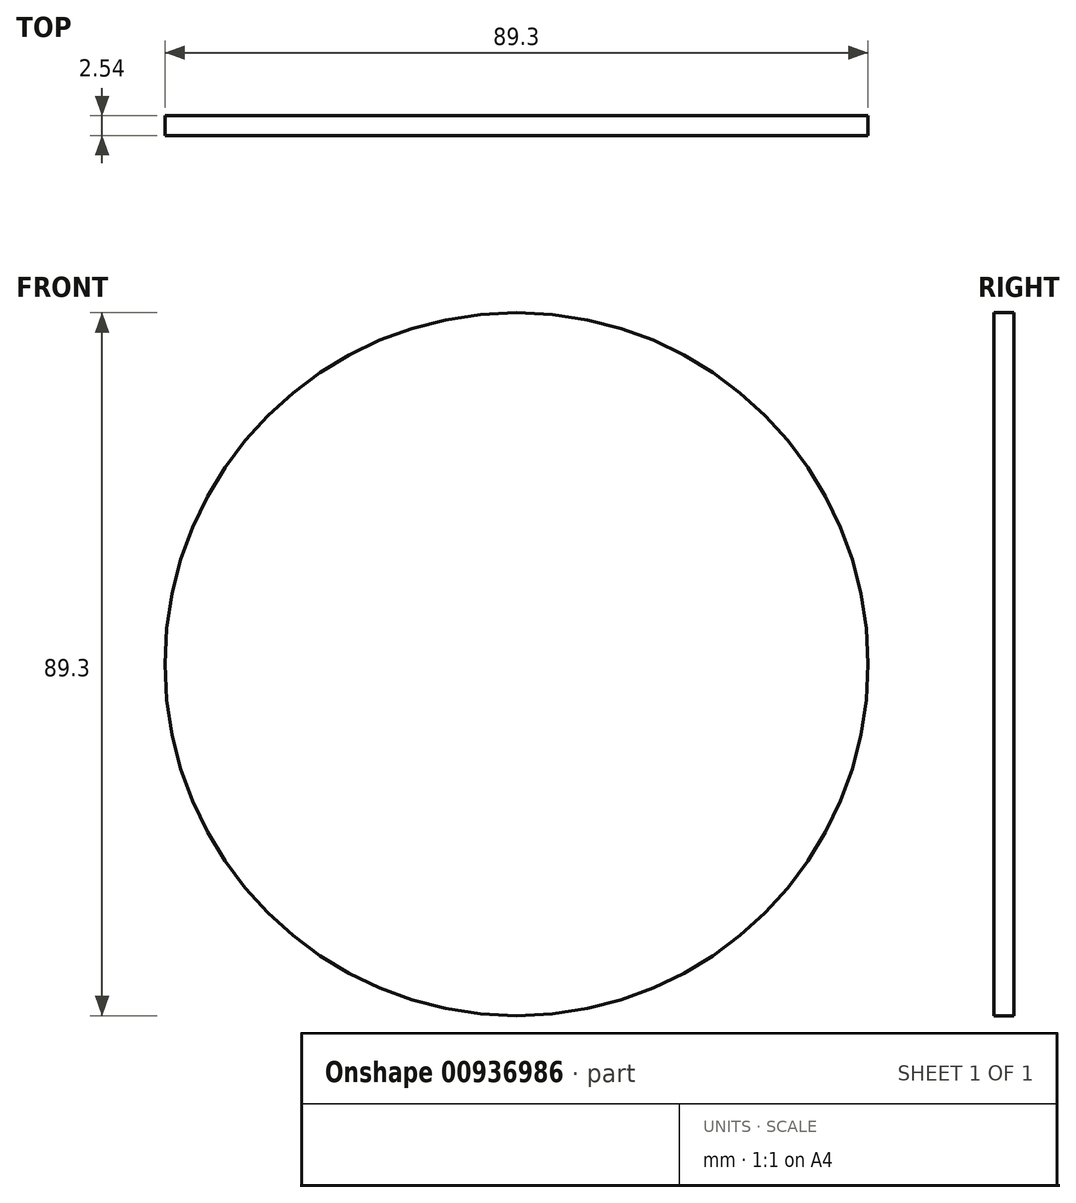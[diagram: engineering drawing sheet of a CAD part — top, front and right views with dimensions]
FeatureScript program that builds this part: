
annotation { "Feature Type Name" : "Feature", "Feature Type Description" : "" }
export const myFeature = defineFeature(function(context is Context, id is Id, definition is map)
    precondition{}
    {
        {
            var Q0;
            Q0=qCreatedBy(makeId("Front.planeOp"),FACE);
            var sketch = newSketch(context, id + "F0", { "sketchPlane" : qUnion([Q0])});
            skCircle(sketch, "E0", {"center": v(0, 0) * mm, "radius": 44.65 * mm});
            skSolve(sketch);
        }
        {
            var Q0;
            Q0=makeQuery(id+"F0.imprint","IMPRINT",FACE,{"disambiguationData":[TD([[makeQuery(id+"F0.imprint","IMPRINT",EDGE,{"derivedFrom":sQuery(id+"F0.wireOp",EDGE,"E0")}),1.0]])]});
            extrude(context, id + "F1", {"entities" : qUnion([Q0]), "depth" : 2.54 * mm, "offsetDistance" : 25.4 * mm});
        }
    });
